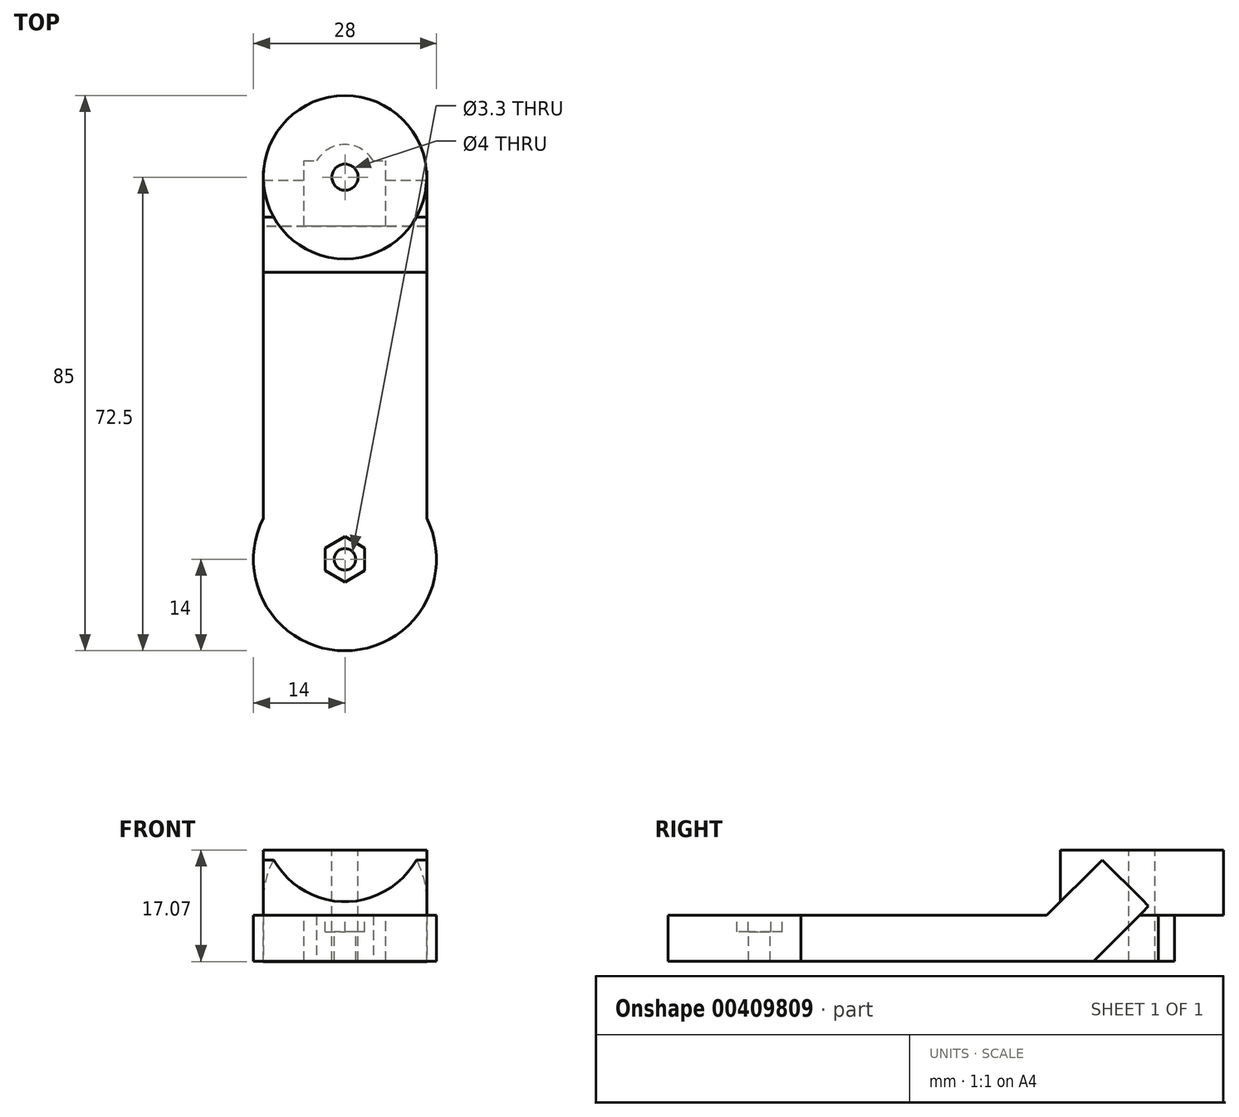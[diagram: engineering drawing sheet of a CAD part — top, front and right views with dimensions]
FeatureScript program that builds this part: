
annotation { "Feature Type Name" : "Feature", "Feature Type Description" : "" }
export const myFeature = defineFeature(function(context is Context, id is Id, definition is map)
    precondition{}
    {
        {
            var Q0;
            Q0=qCreatedBy(makeId("Top.planeOp"),FACE);
            var sketch = newSketch(context, id + "F0", { "sketchPlane" : qUnion([Q0])});
            skLineSegment(sketch, "E0.bottom", {"start": v(12.5, -27.5) * mm, "end": v(-12.5, -27.5) * mm});
            skLineSegment(sketch, "E0.top", {"start": v(12.5, 27.5) * mm, "end": v(-12.5, 27.5) * mm});
            skLineSegment(sketch, "E0.left", {"start": v(12.5, -27.5) * mm, "end": v(12.5, 27.5) * mm});
            skLineSegment(sketch, "E0.right", {"start": v(-12.5, -27.5) * mm, "end": v(-12.5, 27.5) * mm});
            skPoint(sketch, "E0.middle", {"position": v(0, 0) * mm});
            skLineSegment(sketch, "E1", {"start": v(-12.5, 27.5) * mm, "end": v(0, 27.5) * mm, "construction": true});
            skLineSegment(sketch, "E2", {"start": v(12.5, 27.5) * mm, "end": v(0, 27.5) * mm, "construction": true});
            skPoint(sketch, "E3.oppositeSnap0", {"position": v(6.25, 27.5) * mm});
            skLineSegment(sketch, "E3.bottom", {"start": v(-6.25, 27.5) * mm, "end": v(6.25, 27.5) * mm});
            skLineSegment(sketch, "E3.top", {"start": v(-6.25, 37.5) * mm, "end": v(6.25, 37.5) * mm});
            skLineSegment(sketch, "E3.left", {"start": v(-6.25, 27.5) * mm, "end": v(-6.25, 37.5) * mm});
            skLineSegment(sketch, "E3.right", {"start": v(6.25, 27.5) * mm, "end": v(6.25, 37.5) * mm});
            skLineSegment(sketch, "E4", {"start": v(6.25, 37.5) * mm, "end": v(6.25, 35) * mm, "construction": true});
            skLineSegment(sketch, "E5", {"start": v(6.25, 35) * mm, "end": v(0, 35) * mm, "construction": true});
            skCircle(sketch, "E6", {"center": v(0, 35) * mm, "radius": 2.5 * mm, "construction": true});
            skCircle(sketch, "E7", {"center": v(0, 35) * mm, "radius": 5 * mm});
            skSolve(sketch);
        }
        {
            var Q0;
            Q0 = qSketchRegion(id + "F0", true);
            extrude(context, id + "F1", {"entities" : qUnion([Q0]), "depth" : 7 * mm});
        }
        {
            var Q0;
            Q0=makeQuery(id+"F1.opExtrude","CAP_FACE",FACE,{"disambiguationData":[OSD([sQuery(id+"F0.wireOp",EDGE,"E0.bottom"),sQuery(id+"F0.wireOp",EDGE,"E0.top"),sQuery(id+"F0.wireOp",EDGE,"E0.left"),sQuery(id+"F0.wireOp",EDGE,"E0.right"),sQuery(id+"F0.wireOp",EDGE,"E3.left"),sQuery(id+"F0.wireOp",EDGE,"E3.right"),sQuery(id+"F0.wireOp",EDGE,"E7")])],"isStart":false});
            var sketch = newSketch(context, id + "F2", { "sketchPlane" : qUnion([Q0])});
            skCircle(sketch, "E8", {"center": v(0, 35) * mm, "radius": 12.5 * mm});
            skSolve(sketch);
        }
        {
            var Q0;
            Q0 = qSketchRegion(id + "F2", true);
            extrude(context, id + "F3", {"entities" : qUnion([Q0]), "operationType" : NewBodyOperationType.ADD, "depth" : 10 * mm});
        }
        {
            var Q0;
            Q0=makeQuery(id+"F1.opExtrude","CAP_FACE",FACE,{"disambiguationData":[OSD([sQuery(id+"F0.wireOp",EDGE,"E0.bottom"),sQuery(id+"F0.wireOp",EDGE,"E0.top"),sQuery(id+"F0.wireOp",EDGE,"E0.left"),sQuery(id+"F0.wireOp",EDGE,"E0.right"),sQuery(id+"F0.wireOp",EDGE,"E3.left"),sQuery(id+"F0.wireOp",EDGE,"E3.right"),sQuery(id+"F0.wireOp",EDGE,"E7")])],"isStart":false});
            var sketch = newSketch(context, id + "F4", { "sketchPlane" : qUnion([Q0])});
            skLineSegment(sketch, "E9", {"start": v(12.5, -27.5) * mm, "end": v(12.5, -19.5) * mm, "construction": true});
            skLineSegment(sketch, "E10", {"start": v(12.5, -19.5) * mm, "end": v(-12.5, -19.5) * mm, "construction": true});
            skLineSegment(sketch, "E11", {"start": v(12.5, -27.5) * mm, "end": v(-12.5, -19.5) * mm, "construction": true});
            skCircle(sketch, "E12", {"center": v(0, -23.5) * mm, "radius": 2 * mm});
            skSolve(sketch);
        }
        {
            var Q0;
            Q0 = qSketchRegion(id + "F4", true);
            extrude(context, id + "F5", {"entities" : qUnion([Q0]), "operationType" : NewBodyOperationType.REMOVE, "endBound" : BoundingType.UP_TO_NEXT, "oppositeDirection" : true, "depth" : 25 * mm});
        }
        {
            var Q0;
            Q0=makeQuery(id+"F1.opExtrude","CAP_FACE",FACE,{"disambiguationData":[OSD([sQuery(id+"F0.wireOp",EDGE,"E0.bottom"),sQuery(id+"F0.wireOp",EDGE,"E0.top"),sQuery(id+"F0.wireOp",EDGE,"E0.left"),sQuery(id+"F0.wireOp",EDGE,"E0.right"),sQuery(id+"F0.wireOp",EDGE,"E3.left"),sQuery(id+"F0.wireOp",EDGE,"E3.right"),sQuery(id+"F0.wireOp",EDGE,"E7")])],"isStart":false});
            var sketch = newSketch(context, id + "F6", { "sketchPlane" : qUnion([Q0])});
            skLineSegment(sketch, "E13", {"start": v(12.5, 27.5) * mm, "end": v(-12.5, 27.5) * mm, "construction": true});
            skSolve(sketch);
        }
        {
            var Q0;
            Q0=sQuery(id+"F6.wireOp",EDGE,"E13");
            cPlane(context, id + "F7", {"entities" : qUnion([Q0]), "cplaneType" : CPlaneType.LINE_ANGLE, "offset" : 25 * mm, "angle" : 45 * degree, "width" : 150 * mm, "height" : 150 * mm});
        }
        {
            var Q0;
            Q0=qCreatedBy(id+"F7.planeOp",FACE);
            cPlane(context, id + "F8", {"entities" : qUnion([Q0]), "cplaneType" : CPlaneType.OFFSET, "offset" : 5 * mm, "width" : 150 * mm, "height" : 150 * mm});
        }
        {
            var Q0;
            Q0=qCreatedBy(id+"F8.planeOp",FACE);
            var sketch = newSketch(context, id + "F9", { "sketchPlane" : qUnion([Q0])});
            skLineSegment(sketch, "E14", {"start": v(12.5, 19.4) * mm, "end": v(-12.5, 19.4) * mm});
            skLineSegment(sketch, "E15.bottom", {"start": v(-12.5, 19.4) * mm, "end": v(12.5, 19.4) * mm});
            skLineSegment(sketch, "E15.top", {"start": v(-12.5, 31.4) * mm, "end": v(12.5, 31.4) * mm});
            skLineSegment(sketch, "E15.left", {"start": v(-12.5, 19.4) * mm, "end": v(-12.5, 31.4) * mm});
            skLineSegment(sketch, "E15.right", {"start": v(12.5, 19.4) * mm, "end": v(12.5, 31.4) * mm});
            skSolve(sketch);
        }
        {
            var Q0;
            Q0 = qSketchRegion(id + "F9", true);
            var Q1;
            Q1=makeQuery(id+"F1.opExtrude","SWEPT_BODY",BODY,{"disambiguationData":[OSD([sQuery(id+"F0.wireOp",EDGE,"E0.bottom"),sQuery(id+"F0.wireOp",EDGE,"E0.top"),sQuery(id+"F0.wireOp",EDGE,"E0.left"),sQuery(id+"F0.wireOp",EDGE,"E0.right"),sQuery(id+"F0.wireOp",EDGE,"E3.left"),sQuery(id+"F0.wireOp",EDGE,"E3.right"),sQuery(id+"F0.wireOp",EDGE,"E7")])]});
            extrude(context, id + "F10", {"entities" : qUnion([Q0]), "operationType" : NewBodyOperationType.ADD, "oppositeDirection" : true, "endBoundEntityBody" : qUnion([Q1]), "depth" : 10 * mm});
        }
        {
            var Q0;
            Q0=makeQuery(id+"F3.opExtrude","CAP_FACE",FACE,{"disambiguationData":[OSD([sQuery(id+"F2.wireOp",EDGE,"E8")])],"isStart":false});
            var sketch = newSketch(context, id + "F11", { "sketchPlane" : qUnion([Q0])});
            skCircle(sketch, "E16", {"center": v(0, 35) * mm, "radius": 2 * mm});
            skSolve(sketch);
        }
        {
            var Q0;
            Q0 = qSketchRegion(id + "F11", true);
            extrude(context, id + "F12", {"entities" : qUnion([Q0]), "operationType" : NewBodyOperationType.REMOVE, "endBound" : BoundingType.UP_TO_NEXT, "oppositeDirection" : true, "depth" : 25 * mm});
        }
        {
            var Q0;
            {var subQ0=sQuery(id+"F0.wireOp",EDGE,"E0.right");var subQ1=sQuery(id+"F0.wireOp",EDGE,"E0.left");var subQ2=sQuery(id+"F0.wireOp",EDGE,"E0.bottom");Q0=makeQuery(id+"F10.boolean.opBoolean","SPLIT",FACE,{"disambiguationData":[TD([makeQuery(id+"F1.opExtrude","SWEPT_FACE",FACE,{"disambiguationData":[OSD([subQ2])]})])],"derivedFrom":makeQuery(id+"F1.opExtrude","CAP_FACE",FACE,{"disambiguationData":[OSD([subQ2,sQuery(id+"F0.wireOp",EDGE,"E0.top"),subQ1,subQ0,sQuery(id+"F0.wireOp",EDGE,"E3.top"),sQuery(id+"F0.wireOp",EDGE,"E3.left"),sQuery(id+"F0.wireOp",EDGE,"E3.right"),sQuery(id+"F0.wireOp",EDGE,"E7")])],"isStart":true})});}
            var sketch = newSketch(context, id + "F13", { "sketchPlane" : qUnion([Q0])});
            skCircle(sketch, "E17", {"center": v(0, 23.5) * mm, "radius": 14 * mm});
            skSolve(sketch);
        }
        {
            var Q0;
            Q0 = qSketchRegion(id + "F13", true);
            var Q1;
            Q1=makeQuery(id+"F1.opExtrude","CAP_FACE",FACE,{"disambiguationData":[OSD([sQuery(id+"F0.wireOp",EDGE,"E0.bottom"),sQuery(id+"F0.wireOp",EDGE,"E0.top"),sQuery(id+"F0.wireOp",EDGE,"E0.left"),sQuery(id+"F0.wireOp",EDGE,"E0.right"),sQuery(id+"F0.wireOp",EDGE,"E3.top"),sQuery(id+"F0.wireOp",EDGE,"E3.left"),sQuery(id+"F0.wireOp",EDGE,"E3.right"),sQuery(id+"F0.wireOp",EDGE,"E7")])],"isStart":false});
            extrude(context, id + "F14", {"entities" : qUnion([Q0]), "operationType" : NewBodyOperationType.ADD, "endBound" : BoundingType.UP_TO_SURFACE, "oppositeDirection" : true, "endBoundEntityFace" : qUnion([Q1]), "depth" : 25 * mm});
        }
        {
            var Q0;
            {var subQ0=sQuery(id+"F0.wireOp",EDGE,"E7");var subQ1=sQuery(id+"F0.wireOp",EDGE,"E3.right");var subQ2=sQuery(id+"F0.wireOp",EDGE,"E3.left");var subQ3=sQuery(id+"F0.wireOp",EDGE,"E3.top");var subQ4=sQuery(id+"F0.wireOp",EDGE,"E0.right");var subQ5=sQuery(id+"F0.wireOp",EDGE,"E0.left");var subQ6=sQuery(id+"F0.wireOp",EDGE,"E0.top");var subQ7=sQuery(id+"F0.wireOp",EDGE,"E0.bottom");Q0=makeQuery(id+"F14.boolean.opBoolean","MERGE",FACE,{"derivedFrom":[makeQuery(id+"F1.opExtrude","CAP_FACE",FACE,{"disambiguationData":[OSD([subQ7,subQ6,subQ5,subQ4,subQ3,subQ2,subQ1,subQ0])],"isStart":false}),makeQuery(id+"F14.opExtrude","CAP_FACE",FACE,{"disambiguationData":[OSD([subQ7,subQ6,subQ5,subQ4,subQ3,subQ2,subQ1,subQ0])],"isStart":false})]});}
            var sketch = newSketch(context, id + "F15", { "sketchPlane" : qUnion([Q0])});
            skCircle(sketch, "E18", {"center": v(0, -23.5) * mm, "radius": 1.65 * mm});
            skSolve(sketch);
        }
        {
            var Q0;
            Q0 = qSketchRegion(id + "F15", true);
            extrude(context, id + "F16", {"entities" : qUnion([Q0]), "operationType" : NewBodyOperationType.REMOVE, "endBound" : BoundingType.UP_TO_NEXT, "oppositeDirection" : true, "depth" : 25 * mm});
        }
        {
            var Q0;
            {var subQ0=sQuery(id+"F0.wireOp",EDGE,"E7");var subQ1=sQuery(id+"F0.wireOp",EDGE,"E3.right");var subQ2=sQuery(id+"F0.wireOp",EDGE,"E3.left");var subQ3=sQuery(id+"F0.wireOp",EDGE,"E3.top");var subQ4=sQuery(id+"F0.wireOp",EDGE,"E0.right");var subQ5=sQuery(id+"F0.wireOp",EDGE,"E0.left");var subQ6=sQuery(id+"F0.wireOp",EDGE,"E0.top");var subQ7=sQuery(id+"F0.wireOp",EDGE,"E0.bottom");Q0=makeQuery(id+"F14.boolean.opBoolean","MERGE",FACE,{"derivedFrom":[makeQuery(id+"F1.opExtrude","CAP_FACE",FACE,{"disambiguationData":[OSD([subQ7,subQ6,subQ5,subQ4,subQ3,subQ2,subQ1,subQ0])],"isStart":false}),makeQuery(id+"F14.opExtrude","CAP_FACE",FACE,{"disambiguationData":[OSD([subQ7,subQ6,subQ5,subQ4,subQ3,subQ2,subQ1,subQ0])],"isStart":false})]});}
            var sketch = newSketch(context, id + "F17", { "sketchPlane" : qUnion([Q0])});
            skCircle(sketch, "E19.cCircle", {"center": v(0, -23.5) * mm, "radius": 3 * mm, "construction": true});
            skLineSegment(sketch, "E19.0", {"start": v(3, -25.23) * mm, "end": v(0, -26.96) * mm});
            skLineSegment(sketch, "E19.1", {"start": v(0, -26.96) * mm, "end": v(-3, -25.23) * mm});
            skLineSegment(sketch, "E19.2", {"start": v(-3, -25.23) * mm, "end": v(-3, -21.77) * mm});
            skLineSegment(sketch, "E19.3", {"start": v(-3, -21.77) * mm, "end": v(0, -20.04) * mm});
            skLineSegment(sketch, "E19.4", {"start": v(0, -20.04) * mm, "end": v(3, -21.77) * mm});
            skLineSegment(sketch, "E19.5", {"start": v(3, -21.77) * mm, "end": v(3, -25.23) * mm});
            skPoint(sketch, "E19.0.midPoint", {"position": v(1.5, -26.1) * mm});
            skSolve(sketch);
        }
        {
            var Q0;
            Q0 = qSketchRegion(id + "F17", true);
            extrude(context, id + "F18", {"entities" : qUnion([Q0]), "operationType" : NewBodyOperationType.REMOVE, "oppositeDirection" : true, "depth" : 2.5 * mm});
        }
    });
